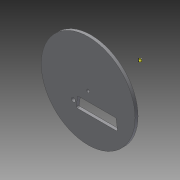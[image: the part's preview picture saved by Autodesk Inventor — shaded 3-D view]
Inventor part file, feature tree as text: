
AUTODESK INVENTOR PART (.ipt)
format: ipt  version: 2015 (Build 190159000, 159)  size: 124,928 bytes
history: native  units: mm
features: extrude x4, sketch x3, chamfer x2, fillet x1
ambient origin geometry x8: Origin, YZ Plane, XZ Plane, XY Plane, X Axis, Y Axis, Z Axis, Center Point
bodies: Solid1 (feature_tree)
feature tree (10):
  extrude  "Extrusion1"  Depth=3.0mm
  extrude  "Extrusion2"  Depth=3.0mm TaperAngle=0.0deg
  extrude  "Extrusion3"  Depth=1.5mm TaperAngle=45.0deg
  chamfer  "Chamfer1"  Distance=1.0mm
  chamfer  "Chamfer2"  Distance=4.0mm
  fillet  "Fillet1"  Radius=3.0mm
  extrude  "Extrusion13"  Depth=10.0mm TaperAngle=0.0deg
  sketch  "Sketch1"  dims[d1=3.0mm d2=0.0mm d3=3.0mm]
  sketch  "Sketch3"  dims[d4=3.765mm d5=0.0mm d10=3.0mm d11=0.0mm]
  sketch  "Sketch15"  dims[d14=45.0deg d15=1.5mm d16=11.0mm d17=45.0deg d18=1.0mm d86=4.0mm d87=3.0mm d88=10.0mm d89=0.0mm]
